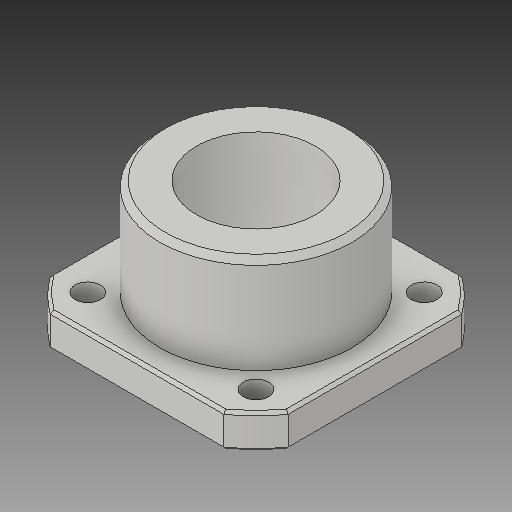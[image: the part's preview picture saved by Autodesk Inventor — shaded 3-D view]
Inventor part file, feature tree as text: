
AUTODESK INVENTOR PART (.ipt)
format: ipt  version: 2018 (Build 220112000, 112)  size: 192,000 bytes
history: native  units: mm
features: sketch x6, extrude x5, chamfer x3
ambient origin geometry x8: Origin, YZ Plane, XZ Plane, XY Plane, X Axis, Y Axis, Z Axis, Center Point
bodies: Solid1 (feature_tree)
feature tree (14):
  extrude  "Extrusion1"  Depth=42.0mm
  extrude  "Extrusion2"  Depth=33.9mm
  extrude  "Extrusion3"  Depth=21.0mm
  sketch  "Sketch4"  dims[d11=76.65mm d12=0.0mm d13=6.5mm]
  extrude  "Extrusion4"  Depth=6.5mm
  chamfer  "Chamfer1"  Distance=40.0mm Angle=360.0deg
  chamfer  "Chamfer2"  Distance=88.15mm
  extrude  "Extrusion5"  Depth=1.0mm TaperAngle=45.0deg
  chamfer  "Chamfer3"  Distance=0.5mm Angle=45.0deg
  sketch  "Sketch1"  dims[d3=42.0mm d4=42.0mm]
  sketch  "Sketch2"  dims[d5=6.0mm d6=0.0mm d7=33.9mm]
  sketch  "Sketch3"  dims[d8=17.1mm d9=0.0mm d10=21.0mm]
  sketch  "Sketch5"  dims[d14=8.0mm]
  sketch  "Sketch6"  dims[d15=4.5mm d16=40.0mm d18=360.0deg d20=88.15mm d21=0.0mm d22=1.0mm d23=2.0mm d24=45.0deg d25=0.5mm d26=2.0mm d27=45.0deg d28=15.5mm d29=219.6mm d30=0.0mm d31=0.5mm d32=2.0mm d33=45.0deg]
